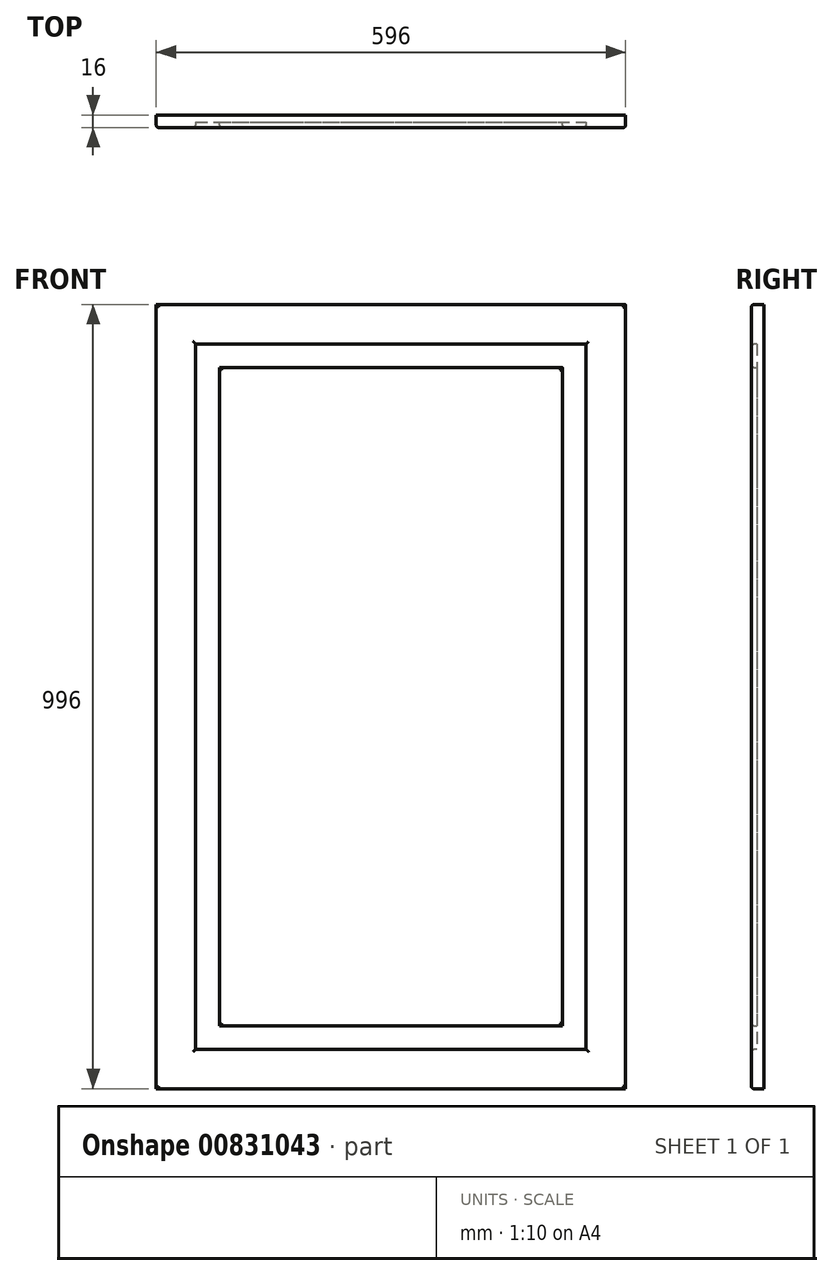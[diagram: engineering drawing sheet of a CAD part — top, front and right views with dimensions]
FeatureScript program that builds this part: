
annotation { "Feature Type Name" : "Feature", "Feature Type Description" : "" }
export const myFeature = defineFeature(function(context is Context, id is Id, definition is map)
    precondition{}
    {
        {
            var Q0;
            Q0=qCreatedBy(makeId("Front.planeOp"),FACE);
            var sketch = newSketch(context, id + "F0", { "sketchPlane" : qUnion([Q0])});
            skLineSegment(sketch, "E0.bottom", {"start": v(0, 0) * mm, "end": v(44.66, 0) * mm});
            skLineSegment(sketch, "E0.top", {"start": v(0, 33.8) * mm, "end": v(44.66, 33.8) * mm});
            skLineSegment(sketch, "E0.left", {"start": v(0, 0) * mm, "end": v(0, 33.8) * mm});
            skLineSegment(sketch, "E0.right", {"start": v(44.66, 0) * mm, "end": v(44.66, 33.8) * mm});
            skSolve(sketch);
        }
        {
            var Q0;
            Q0=makeQuery(id+"F0.imprint","IMPRINT",FACE,{"disambiguationData":[TD([[makeQuery(id+"F0.imprint","IMPRINT",EDGE,{"derivedFrom":sQuery(id+"F0.wireOp",EDGE,"E0.bottom")}),1.0]])]});
            extrude(context, id + "F1", {"entities" : qUnion([Q0]), "depth" : 16 * mm, "offsetDistance" : 25.4 * mm});
        }
        {
            var Q0;
            Q0=makeQuery(id+"F1.opExtrude","SWEPT_FACE",FACE,{"disambiguationData":[OSD([sQuery(id+"F0.wireOp",EDGE,"E0.bottom")])]});
            extrude(context, id + "F2", {"entities" : qUnion([Q0]), "operationType" : NewBodyOperationType.ADD, "oppositeDirection" : true, "depth" : 796 * mm, "offsetDistance" : 25 * mm});
        }
        {
            var Q0;
            {var subQ0=sQuery(id+"F0.wireOp",EDGE,"E0.left");Q0=makeQuery(id+"F2.boolean.opBoolean","MERGE",FACE,{"derivedFrom":[makeQuery(id+"F1.opExtrude","SWEPT_FACE",FACE,{"disambiguationData":[OSD([subQ0])]}),makeQuery(id+"F2.opExtrude","SWEPT_FACE",FACE,{"disambiguationData":[OSD([sQuery(id+"F0.wireOp",EDGE,"E0.bottom"),subQ0])]})]});}
            extrude(context, id + "F3", {"entities" : qUnion([Q0]), "operationType" : NewBodyOperationType.ADD, "oppositeDirection" : true, "depth" : 196 * mm, "offsetDistance" : 25 * mm});
        }
        {
            var Q0;
            {var subQ0=sQuery(id+"F0.wireOp",EDGE,"E0.left");var subQ1=sQuery(id+"F0.wireOp",EDGE,"E0.bottom");Q0=makeQuery(id+"F3.boolean.opBoolean","MERGE",FACE,{"derivedFrom":[makeQuery(id+"F2.boolean.opBoolean","MERGE",FACE,{"derivedFrom":[makeQuery(id+"F1.opExtrude","CAP_FACE",FACE,{"disambiguationData":[OSD([subQ1,sQuery(id+"F0.wireOp",EDGE,"E0.top"),subQ0,sQuery(id+"F0.wireOp",EDGE,"E0.right")])],"isStart":false}),makeQuery(id+"F2.opExtrude","SWEPT_FACE",FACE,{"disambiguationData":[OSD([subQ1]),TDD([makeQuery(id+"F1.opExtrude","CAP_EDGE",EDGE,{"disambiguationData":[OSD([subQ1])],"isStart":false})])]})]}),makeQuery(id+"F3.opExtrude","SWEPT_FACE",FACE,{"disambiguationData":[OSD([subQ1,subQ0]),TDD([makeQuery(id+"F2.boolean.opBoolean","MERGE",EDGE,{"derivedFrom":[makeQuery(id+"F1.opExtrude","CAP_EDGE",EDGE,{"disambiguationData":[OSD([subQ0])],"isStart":false}),makeQuery(id+"F2.opExtrude","SWEPT_EDGE",EDGE,{"disambiguationData":[OSD([subQ1,subQ0]),TDD([makeQuery(id+"F1.opExtrude","CAP_VERTEX",VERTEX,{"disambiguationData":[OSD([subQ1,subQ0])],"isStart":false})])]})]})])]})]});}
            var sketch = newSketch(context, id + "F4", { "sketchPlane" : qUnion([Q0])});
            skLineSegment(sketch, "E1.bottom", {"start": v(59.7, 646.67) * mm, "end": v(128.66, 646.67) * mm});
            skLineSegment(sketch, "E1.top", {"start": v(59.7, 152.97) * mm, "end": v(128.66, 152.97) * mm});
            skLineSegment(sketch, "E1.left", {"start": v(59.7, 646.67) * mm, "end": v(59.7, 152.97) * mm});
            skLineSegment(sketch, "E1.right", {"start": v(128.66, 646.67) * mm, "end": v(128.66, 152.97) * mm});
            skSolve(sketch);
        }
        {
            var Q0;
            Q0=makeQuery(id+"F4.imprint","IMPRINT",FACE,{"disambiguationData":[TD([[makeQuery(id+"F4.imprint","IMPRINT",EDGE,{"derivedFrom":sQuery(id+"F4.wireOp",EDGE,"E1.bottom")}),-1.0]])]});
            extrude(context, id + "F5", {"entities" : qUnion([Q0]), "operationType" : NewBodyOperationType.REMOVE, "oppositeDirection" : true, "depth" : 7 * mm, "offsetDistance" : 25 * mm});
        }
        {
            var Q0;
            Q0=makeQuery(id+"F5.boolean.opBoolean","COPY",FACE,{"derivedFrom":makeQuery(id+"F5.opExtrude","SWEPT_FACE",FACE,{"disambiguationData":[OSD([sQuery(id+"F4.wireOp",EDGE,"E1.left")])]})});
            extrude(context, id + "F6", {"entities" : qUnion([Q0]), "operationType" : NewBodyOperationType.REMOVE, "oppositeDirection" : true, "depth" : 9.7 * mm, "offsetDistance" : 25 * mm});
        }
        {
            var Q0;
            {var subQ0=sQuery(id+"F4.wireOp",EDGE,"E1.bottom");Q0=makeQuery(id+"F6.boolean.opBoolean","MERGE",FACE,{"derivedFrom":[makeQuery(id+"F5.boolean.opBoolean","COPY",FACE,{"derivedFrom":makeQuery(id+"F5.opExtrude","SWEPT_FACE",FACE,{"disambiguationData":[OSD([subQ0])]})}),makeQuery(id+"F6.opExtrude","SWEPT_FACE",FACE,{"disambiguationData":[OSD([subQ0,sQuery(id+"F4.wireOp",EDGE,"E1.left")])]})]});}
            extrude(context, id + "F7", {"entities" : qUnion([Q0]), "operationType" : NewBodyOperationType.ADD, "oppositeDirection" : true, "depth" : 99.33 * mm, "offsetDistance" : 25 * mm});
        }
        {
            var Q0;
            {var subQ0=sQuery(id+"F4.wireOp",EDGE,"E1.bottom");Q0=makeQuery(id+"F6.boolean.opBoolean","MERGE",FACE,{"derivedFrom":[makeQuery(id+"F5.boolean.opBoolean","COPY",FACE,{"derivedFrom":makeQuery(id+"F5.opExtrude","SWEPT_FACE",FACE,{"disambiguationData":[OSD([subQ0])]})}),makeQuery(id+"F6.opExtrude","SWEPT_FACE",FACE,{"disambiguationData":[OSD([subQ0,sQuery(id+"F4.wireOp",EDGE,"E1.left")])]})]});}
            extrude(context, id + "F8", {"entities" : qUnion([Q0]), "operationType" : NewBodyOperationType.REMOVE, "oppositeDirection" : true, "depth" : 99.33 * mm, "offsetDistance" : 25 * mm});
        }
        {
            var Q0;
            {var subQ0=sQuery(id+"F4.wireOp",EDGE,"E1.right");Q0=makeQuery(id+"F8.boolean.opBoolean","MERGE",FACE,{"derivedFrom":[makeQuery(id+"F5.boolean.opBoolean","COPY",FACE,{"derivedFrom":makeQuery(id+"F5.opExtrude","SWEPT_FACE",FACE,{"disambiguationData":[OSD([subQ0])]})}),makeQuery(id+"F8.opExtrude","SWEPT_FACE",FACE,{"disambiguationData":[OSD([sQuery(id+"F4.wireOp",EDGE,"E1.bottom"),subQ0])]})]});}
            extrude(context, id + "F9", {"entities" : qUnion([Q0]), "operationType" : NewBodyOperationType.REMOVE, "oppositeDirection" : true, "depth" : 17.34 * mm, "offsetDistance" : 25 * mm});
        }
        {
            var Q0;
            {var subQ0=sQuery(id+"F4.wireOp",EDGE,"E1.top");Q0=makeQuery(id+"F9.boolean.opBoolean","MERGE",FACE,{"derivedFrom":[makeQuery(id+"F6.boolean.opBoolean","MERGE",FACE,{"derivedFrom":[makeQuery(id+"F5.boolean.opBoolean","COPY",FACE,{"derivedFrom":makeQuery(id+"F5.opExtrude","SWEPT_FACE",FACE,{"disambiguationData":[OSD([subQ0])]})}),makeQuery(id+"F6.opExtrude","SWEPT_FACE",FACE,{"disambiguationData":[OSD([subQ0,sQuery(id+"F4.wireOp",EDGE,"E1.left")])]})]}),makeQuery(id+"F9.opExtrude","SWEPT_FACE",FACE,{"disambiguationData":[OSD([subQ0,sQuery(id+"F4.wireOp",EDGE,"E1.right")])]})]});}
            extrude(context, id + "F10", {"entities" : qUnion([Q0]), "operationType" : NewBodyOperationType.REMOVE, "oppositeDirection" : true, "depth" : 102.97 * mm, "offsetDistance" : 25 * mm});
        }
        {
            var Q0;
            {var subQ0=sQuery(id+"F4.wireOp",EDGE,"E1.right");var subQ1=sQuery(id+"F4.wireOp",EDGE,"E1.top");var subQ2=sQuery(id+"F4.wireOp",EDGE,"E1.left");var subQ3=sQuery(id+"F4.wireOp",EDGE,"E1.bottom");Q0=makeQuery(id+"F10.boolean.opBoolean","MERGE",FACE,{"derivedFrom":[makeQuery(id+"F9.boolean.opBoolean","MERGE",FACE,{"derivedFrom":[makeQuery(id+"F8.boolean.opBoolean","MERGE",FACE,{"derivedFrom":[makeQuery(id+"F6.boolean.opBoolean","MERGE",FACE,{"derivedFrom":[makeQuery(id+"F5.boolean.opBoolean","COPY",FACE,{"derivedFrom":makeQuery(id+"F5.opExtrude","CAP_FACE",FACE,{"disambiguationData":[OSD([subQ3,subQ1,subQ2,subQ0])],"isStart":false})}),makeQuery(id+"F6.opExtrude","SWEPT_FACE",FACE,{"disambiguationData":[OSD([subQ2]),TDD([makeQuery(id+"F5.boolean.opBoolean","COPY",EDGE,{"derivedFrom":makeQuery(id+"F5.opExtrude","CAP_EDGE",EDGE,{"disambiguationData":[OSD([subQ2])],"isStart":false})})])]})]}),makeQuery(id+"F8.opExtrude","SWEPT_FACE",FACE,{"disambiguationData":[OSD([subQ3,subQ2]),TDD([makeQuery(id+"F6.boolean.opBoolean","MERGE",EDGE,{"derivedFrom":[makeQuery(id+"F5.boolean.opBoolean","COPY",EDGE,{"derivedFrom":makeQuery(id+"F5.opExtrude","CAP_EDGE",EDGE,{"disambiguationData":[OSD([subQ3])],"isStart":false})}),makeQuery(id+"F6.opExtrude","SWEPT_EDGE",EDGE,{"disambiguationData":[OSD([subQ3,subQ2]),TDD([makeQuery(id+"F5.boolean.opBoolean","COPY",VERTEX,{"derivedFrom":makeQuery(id+"F5.opExtrude","CAP_VERTEX",VERTEX,{"disambiguationData":[OSD([subQ3,subQ2])],"isStart":false})})])]})]})])]})]}),makeQuery(id+"F9.opExtrude","SWEPT_FACE",FACE,{"disambiguationData":[OSD([subQ3,subQ0]),TDD([makeQuery(id+"F8.boolean.opBoolean","MERGE",EDGE,{"derivedFrom":[makeQuery(id+"F5.boolean.opBoolean","COPY",EDGE,{"derivedFrom":makeQuery(id+"F5.opExtrude","CAP_EDGE",EDGE,{"disambiguationData":[OSD([subQ0])],"isStart":false})}),makeQuery(id+"F8.opExtrude","SWEPT_EDGE",EDGE,{"disambiguationData":[OSD([subQ3,subQ0]),TDD([makeQuery(id+"F5.boolean.opBoolean","COPY",VERTEX,{"derivedFrom":makeQuery(id+"F5.opExtrude","CAP_VERTEX",VERTEX,{"disambiguationData":[OSD([subQ3,subQ0])],"isStart":false})})])]})]})])]})]}),makeQuery(id+"F10.opExtrude","SWEPT_FACE",FACE,{"disambiguationData":[OSD([subQ1,subQ2,subQ0]),TDD([makeQuery(id+"F9.boolean.opBoolean","MERGE",EDGE,{"derivedFrom":[makeQuery(id+"F6.boolean.opBoolean","MERGE",EDGE,{"derivedFrom":[makeQuery(id+"F5.boolean.opBoolean","COPY",EDGE,{"derivedFrom":makeQuery(id+"F5.opExtrude","CAP_EDGE",EDGE,{"disambiguationData":[OSD([subQ1])],"isStart":false})}),makeQuery(id+"F6.opExtrude","SWEPT_EDGE",EDGE,{"disambiguationData":[OSD([subQ1,subQ2]),TDD([makeQuery(id+"F5.boolean.opBoolean","COPY",VERTEX,{"derivedFrom":makeQuery(id+"F5.opExtrude","CAP_VERTEX",VERTEX,{"disambiguationData":[OSD([subQ1,subQ2])],"isStart":false})})])]})]}),makeQuery(id+"F9.opExtrude","SWEPT_EDGE",EDGE,{"disambiguationData":[OSD([subQ1,subQ0]),TDD([makeQuery(id+"F5.boolean.opBoolean","COPY",VERTEX,{"derivedFrom":makeQuery(id+"F5.opExtrude","CAP_VERTEX",VERTEX,{"disambiguationData":[OSD([subQ1,subQ0])],"isStart":false})})])]})]})])]})]});}
            var sketch = newSketch(context, id + "F11", { "sketchPlane" : qUnion([Q0])});
            skLineSegment(sketch, "E2.bottom", {"start": v(74.13, 678.73) * mm, "end": v(109.41, 678.73) * mm});
            skLineSegment(sketch, "E2.top", {"start": v(74.13, 186.63) * mm, "end": v(109.41, 186.63) * mm});
            skLineSegment(sketch, "E2.left", {"start": v(74.13, 678.73) * mm, "end": v(74.13, 186.63) * mm});
            skLineSegment(sketch, "E2.right", {"start": v(109.41, 678.73) * mm, "end": v(109.41, 186.63) * mm});
            skSolve(sketch);
        }
        {
            var Q0;
            Q0=makeQuery(id+"F11.imprint","IMPRINT",FACE,{"disambiguationData":[TD([[makeQuery(id+"F11.imprint","IMPRINT",EDGE,{"derivedFrom":sQuery(id+"F11.wireOp",EDGE,"E2.bottom")}),-1.0]])]});
            extrude(context, id + "F12", {"entities" : qUnion([Q0]), "operationType" : NewBodyOperationType.ADD, "depth" : 7 * mm, "offsetDistance" : 25 * mm});
        }
        {
            var Q0;
            Q0=makeQuery(id+"F12.opExtrude","SWEPT_FACE",FACE,{"disambiguationData":[OSD([sQuery(id+"F11.wireOp",EDGE,"E2.bottom")])]});
            extrude(context, id + "F13", {"entities" : qUnion([Q0]), "operationType" : NewBodyOperationType.ADD, "depth" : 37.27 * mm, "offsetDistance" : 25 * mm});
        }
        {
            var Q0;
            {var subQ0=sQuery(id+"F11.wireOp",EDGE,"E2.right");Q0=makeQuery(id+"F13.boolean.opBoolean","MERGE",FACE,{"derivedFrom":[makeQuery(id+"F12.opExtrude","SWEPT_FACE",FACE,{"disambiguationData":[OSD([subQ0])]}),makeQuery(id+"F13.opExtrude","SWEPT_FACE",FACE,{"disambiguationData":[OSD([sQuery(id+"F11.wireOp",EDGE,"E2.bottom"),subQ0])]})]});}
            extrude(context, id + "F14", {"entities" : qUnion([Q0]), "operationType" : NewBodyOperationType.ADD, "depth" : 6.58 * mm, "offsetDistance" : 25 * mm});
        }
        {
            var Q0;
            {var subQ0=sQuery(id+"F11.wireOp",EDGE,"E2.top");Q0=makeQuery(id+"F14.boolean.opBoolean","MERGE",FACE,{"derivedFrom":[makeQuery(id+"F12.opExtrude","SWEPT_FACE",FACE,{"disambiguationData":[OSD([subQ0])]}),makeQuery(id+"F14.opExtrude","SWEPT_FACE",FACE,{"disambiguationData":[OSD([subQ0,sQuery(id+"F11.wireOp",EDGE,"E2.right")])]})]});}
            extrude(context, id + "F15", {"entities" : qUnion([Q0]), "operationType" : NewBodyOperationType.ADD, "depth" : 106.63 * mm, "offsetDistance" : 25 * mm});
        }
        {
            var Q0;
            {var subQ0=sQuery(id+"F11.wireOp",EDGE,"E2.left");Q0=makeQuery(id+"F15.boolean.opBoolean","MERGE",FACE,{"derivedFrom":[makeQuery(id+"F13.boolean.opBoolean","MERGE",FACE,{"derivedFrom":[makeQuery(id+"F12.opExtrude","SWEPT_FACE",FACE,{"disambiguationData":[OSD([subQ0])]}),makeQuery(id+"F13.opExtrude","SWEPT_FACE",FACE,{"disambiguationData":[OSD([sQuery(id+"F11.wireOp",EDGE,"E2.bottom"),subQ0])]})]}),makeQuery(id+"F15.opExtrude","SWEPT_FACE",FACE,{"disambiguationData":[OSD([sQuery(id+"F11.wireOp",EDGE,"E2.top"),subQ0])]})]});}
            extrude(context, id + "F16", {"entities" : qUnion([Q0]), "operationType" : NewBodyOperationType.REMOVE, "oppositeDirection" : true, "depth" : 5.87 * mm, "offsetDistance" : 25 * mm});
        }
        {
            var Q0;
            Q0=makeQuery(id+"F3.opExtrude","CAP_FACE",FACE,{"disambiguationData":[OSD([sQuery(id+"F0.wireOp",EDGE,"E0.bottom"),sQuery(id+"F0.wireOp",EDGE,"E0.left")])],"isStart":false});
            extrude(context, id + "F17", {"entities" : qUnion([Q0]), "operationType" : NewBodyOperationType.ADD, "depth" : 200 * mm, "offsetDistance" : 25 * mm});
        }
        {
            var Q0;
            {var subQ0=sQuery(id+"F4.wireOp",EDGE,"E1.right");Q0=makeQuery(id+"F10.boolean.opBoolean","MERGE",FACE,{"derivedFrom":[makeQuery(id+"F9.boolean.opBoolean","COPY",FACE,{"derivedFrom":makeQuery(id+"F9.opExtrude","CAP_FACE",FACE,{"disambiguationData":[OSD([sQuery(id+"F4.wireOp",EDGE,"E1.bottom"),subQ0])],"isStart":false})}),makeQuery(id+"F10.opExtrude","SWEPT_FACE",FACE,{"disambiguationData":[OSD([sQuery(id+"F4.wireOp",EDGE,"E1.top"),subQ0])]})]});}
            extrude(context, id + "F18", {"entities" : qUnion([Q0]), "operationType" : NewBodyOperationType.REMOVE, "oppositeDirection" : true, "depth" : 200 * mm, "offsetDistance" : 25 * mm});
        }
        {
            var Q0;
            {var subQ0=sQuery(id+"F11.wireOp",EDGE,"E2.right");var subQ1=sQuery(id+"F11.wireOp",EDGE,"E2.top");Q0=makeQuery(id+"F15.boolean.opBoolean","MERGE",FACE,{"derivedFrom":[makeQuery(id+"F14.opExtrude","CAP_FACE",FACE,{"disambiguationData":[OSD([sQuery(id+"F11.wireOp",EDGE,"E2.bottom"),subQ0])],"isStart":false}),makeQuery(id+"F15.opExtrude","SWEPT_FACE",FACE,{"disambiguationData":[OSD([subQ1,subQ0]),TDD([makeQuery(id+"F14.opExtrude","CAP_EDGE",EDGE,{"disambiguationData":[OSD([subQ1,subQ0])],"isStart":false})])]})]});}
            extrude(context, id + "F19", {"entities" : qUnion([Q0]), "operationType" : NewBodyOperationType.ADD, "depth" : 200 * mm, "offsetDistance" : 25 * mm});
        }
        {
            var Q0;
            Q0=makeQuery(id+"F17.opExtrude","CAP_FACE",FACE,{"disambiguationData":[OSD([sQuery(id+"F0.wireOp",EDGE,"E0.bottom"),sQuery(id+"F0.wireOp",EDGE,"E0.left")])],"isStart":false});
            extrude(context, id + "F20", {"entities" : qUnion([Q0]), "operationType" : NewBodyOperationType.ADD, "depth" : 200 * mm, "offsetDistance" : 25 * mm});
        }
        {
            var Q0;
            Q0=makeQuery(id+"F18.boolean.opBoolean","COPY",FACE,{"derivedFrom":makeQuery(id+"F18.opExtrude","CAP_FACE",FACE,{"disambiguationData":[OSD([sQuery(id+"F4.wireOp",EDGE,"E1.bottom"),sQuery(id+"F4.wireOp",EDGE,"E1.top"),sQuery(id+"F4.wireOp",EDGE,"E1.right")])],"isStart":false})});
            extrude(context, id + "F21", {"entities" : qUnion([Q0]), "operationType" : NewBodyOperationType.REMOVE, "oppositeDirection" : true, "depth" : 200 * mm, "offsetDistance" : 25 * mm});
        }
        {
            var Q0;
            Q0=makeQuery(id+"F19.opExtrude","CAP_FACE",FACE,{"disambiguationData":[OSD([sQuery(id+"F11.wireOp",EDGE,"E2.bottom"),sQuery(id+"F11.wireOp",EDGE,"E2.top"),sQuery(id+"F11.wireOp",EDGE,"E2.right")])],"isStart":false});
            extrude(context, id + "F22", {"entities" : qUnion([Q0]), "operationType" : NewBodyOperationType.ADD, "depth" : 200 * mm, "offsetDistance" : 25 * mm});
        }
        {
            var Q0;
            {var subQ0=sQuery(id+"F0.wireOp",EDGE,"E0.left");var subQ1=sQuery(id+"F0.wireOp",EDGE,"E0.bottom");var subQ2=makeQuery(id+"F2.opExtrude","CAP_EDGE",EDGE,{"disambiguationData":[OSD([subQ1,subQ0])],"isStart":false});var subQ3=makeQuery(id+"F3.opExtrude","CAP_EDGE",EDGE,{"disambiguationData":[OSD([subQ1,subQ0]),TDD([subQ2])],"isStart":false});Q0=makeQuery(id+"F20.boolean.opBoolean","MERGE",FACE,{"derivedFrom":[makeQuery(id+"F17.boolean.opBoolean","MERGE",FACE,{"derivedFrom":[makeQuery(id+"F3.boolean.opBoolean","MERGE",FACE,{"derivedFrom":[makeQuery(id+"F2.opExtrude","CAP_FACE",FACE,{"disambiguationData":[OSD([subQ1])],"isStart":false}),makeQuery(id+"F3.opExtrude","SWEPT_FACE",FACE,{"disambiguationData":[OSD([subQ1,subQ0]),TDD([subQ2])]})]}),makeQuery(id+"F17.opExtrude","SWEPT_FACE",FACE,{"disambiguationData":[OSD([subQ1,subQ0]),TDD([subQ3])]})]}),makeQuery(id+"F20.opExtrude","SWEPT_FACE",FACE,{"disambiguationData":[OSD([subQ1,subQ0]),TDD([makeQuery(id+"F17.opExtrude","CAP_EDGE",EDGE,{"disambiguationData":[OSD([subQ1,subQ0]),TDD([subQ3])],"isStart":false})])]})]});}
            extrude(context, id + "F23", {"entities" : qUnion([Q0]), "operationType" : NewBodyOperationType.ADD, "depth" : 200 * mm, "offsetDistance" : 25 * mm});
        }
        {
            var Q0;
            {var subQ0=sQuery(id+"F4.wireOp",EDGE,"E1.right");var subQ1=sQuery(id+"F4.wireOp",EDGE,"E1.bottom");Q0=makeQuery(id+"F21.boolean.opBoolean","MERGE",FACE,{"derivedFrom":[makeQuery(id+"F18.boolean.opBoolean","MERGE",FACE,{"derivedFrom":[makeQuery(id+"F9.boolean.opBoolean","MERGE",FACE,{"derivedFrom":[makeQuery(id+"F8.boolean.opBoolean","COPY",FACE,{"derivedFrom":makeQuery(id+"F8.opExtrude","CAP_FACE",FACE,{"disambiguationData":[OSD([subQ1,sQuery(id+"F4.wireOp",EDGE,"E1.left")])],"isStart":false})}),makeQuery(id+"F9.opExtrude","SWEPT_FACE",FACE,{"disambiguationData":[OSD([subQ1,subQ0]),TDD([makeQuery(id+"F8.boolean.opBoolean","COPY",EDGE,{"derivedFrom":makeQuery(id+"F8.opExtrude","CAP_EDGE",EDGE,{"disambiguationData":[OSD([subQ1,subQ0])],"isStart":false})})])]})]}),makeQuery(id+"F18.opExtrude","SWEPT_FACE",FACE,{"disambiguationData":[OSD([subQ1,subQ0])]})]}),makeQuery(id+"F21.opExtrude","SWEPT_FACE",FACE,{"disambiguationData":[OSD([subQ1,subQ0])]})]});}
            extrude(context, id + "F24", {"entities" : qUnion([Q0]), "operationType" : NewBodyOperationType.REMOVE, "oppositeDirection" : true, "depth" : 200 * mm, "offsetDistance" : 25 * mm});
        }
        {
            var Q0;
            {var subQ0=sQuery(id+"F11.wireOp",EDGE,"E2.right");var subQ1=sQuery(id+"F11.wireOp",EDGE,"E2.bottom");Q0=makeQuery(id+"F22.boolean.opBoolean","MERGE",FACE,{"derivedFrom":[makeQuery(id+"F19.boolean.opBoolean","MERGE",FACE,{"derivedFrom":[makeQuery(id+"F14.boolean.opBoolean","MERGE",FACE,{"derivedFrom":[makeQuery(id+"F13.opExtrude","CAP_FACE",FACE,{"disambiguationData":[OSD([subQ1])],"isStart":false}),makeQuery(id+"F14.opExtrude","SWEPT_FACE",FACE,{"disambiguationData":[OSD([subQ1,subQ0]),TDD([makeQuery(id+"F13.opExtrude","CAP_EDGE",EDGE,{"disambiguationData":[OSD([subQ1,subQ0])],"isStart":false})])]})]}),makeQuery(id+"F19.opExtrude","SWEPT_FACE",FACE,{"disambiguationData":[OSD([subQ1,subQ0])]})]}),makeQuery(id+"F22.opExtrude","SWEPT_FACE",FACE,{"disambiguationData":[OSD([subQ1,subQ0])]})]});}
            extrude(context, id + "F25", {"entities" : qUnion([Q0]), "operationType" : NewBodyOperationType.ADD, "depth" : 200 * mm, "offsetDistance" : 25 * mm});
        }
        {
            var Q0;
            {var subQ0=sQuery(id+"F0.wireOp",EDGE,"E0.left");var subQ1=sQuery(id+"F0.wireOp",EDGE,"E0.bottom");var subQ2=makeQuery(id+"F1.opExtrude","CAP_VERTEX",VERTEX,{"disambiguationData":[OSD([subQ1,subQ0])],"isStart":false});var subQ3=makeQuery(id+"F2.opExtrude","CAP_VERTEX",VERTEX,{"disambiguationData":[OSD([subQ1,subQ0]),TDD([subQ2])],"isStart":false});var subQ4=makeQuery(id+"F3.opExtrude","CAP_VERTEX",VERTEX,{"disambiguationData":[OSD([subQ1,subQ0]),TDD([subQ3])],"isStart":false});var subQ5=makeQuery(id+"F1.opExtrude","CAP_EDGE",EDGE,{"disambiguationData":[OSD([subQ1])],"isStart":false});var subQ6=makeQuery(id+"F2.boolean.opBoolean","MERGE",EDGE,{"derivedFrom":[makeQuery(id+"F1.opExtrude","CAP_EDGE",EDGE,{"disambiguationData":[OSD([subQ0])],"isStart":false}),makeQuery(id+"F2.opExtrude","SWEPT_EDGE",EDGE,{"disambiguationData":[OSD([subQ1,subQ0]),TDD([subQ2])]})]});var subQ7=makeQuery(id+"F3.opExtrude","CAP_EDGE",EDGE,{"disambiguationData":[OSD([subQ1,subQ0]),TDD([subQ6])],"isStart":false});Q0=makeQuery(id+"F23.boolean.opBoolean","MERGE",FACE,{"derivedFrom":[makeQuery(id+"F20.boolean.opBoolean","MERGE",FACE,{"derivedFrom":[makeQuery(id+"F17.boolean.opBoolean","MERGE",FACE,{"derivedFrom":[makeQuery(id+"F3.boolean.opBoolean","MERGE",FACE,{"derivedFrom":[makeQuery(id+"F2.boolean.opBoolean","MERGE",FACE,{"derivedFrom":[makeQuery(id+"F1.opExtrude","CAP_FACE",FACE,{"disambiguationData":[OSD([subQ1,sQuery(id+"F0.wireOp",EDGE,"E0.top"),subQ0,sQuery(id+"F0.wireOp",EDGE,"E0.right")])],"isStart":false}),makeQuery(id+"F2.opExtrude","SWEPT_FACE",FACE,{"disambiguationData":[OSD([subQ1]),TDD([subQ5])]})]}),makeQuery(id+"F3.opExtrude","SWEPT_FACE",FACE,{"disambiguationData":[OSD([subQ1,subQ0]),TDD([subQ6])]})]}),makeQuery(id+"F17.opExtrude","SWEPT_FACE",FACE,{"disambiguationData":[OSD([subQ1,subQ0]),TDD([subQ7])]})]}),makeQuery(id+"F20.opExtrude","SWEPT_FACE",FACE,{"disambiguationData":[OSD([subQ1,subQ0]),TDD([makeQuery(id+"F17.opExtrude","CAP_EDGE",EDGE,{"disambiguationData":[OSD([subQ1,subQ0]),TDD([subQ7])],"isStart":false})])]})]}),makeQuery(id+"F23.opExtrude","SWEPT_FACE",FACE,{"disambiguationData":[OSD([subQ1,subQ0]),TDD([makeQuery(id+"F20.boolean.opBoolean","MERGE",EDGE,{"derivedFrom":[makeQuery(id+"F17.boolean.opBoolean","MERGE",EDGE,{"derivedFrom":[makeQuery(id+"F3.boolean.opBoolean","MERGE",EDGE,{"derivedFrom":[makeQuery(id+"F2.opExtrude","CAP_EDGE",EDGE,{"disambiguationData":[OSD([subQ1]),TDD([subQ5])],"isStart":false}),makeQuery(id+"F3.opExtrude","SWEPT_EDGE",EDGE,{"disambiguationData":[OSD([subQ1,subQ0]),TDD([subQ3])]})]}),makeQuery(id+"F17.opExtrude","SWEPT_EDGE",EDGE,{"disambiguationData":[OSD([subQ1,subQ0]),TDD([subQ4])]})]}),makeQuery(id+"F20.opExtrude","SWEPT_EDGE",EDGE,{"disambiguationData":[OSD([subQ1,subQ0]),TDD([makeQuery(id+"F17.opExtrude","CAP_VERTEX",VERTEX,{"disambiguationData":[OSD([subQ1,subQ0]),TDD([subQ4])],"isStart":false})])]})]})])]})]});}
            var Q1;
            {var subQ0=sQuery(id+"F11.wireOp",EDGE,"E2.right");var subQ1=sQuery(id+"F11.wireOp",EDGE,"E2.bottom");var subQ2=makeQuery(id+"F12.opExtrude","CAP_VERTEX",VERTEX,{"disambiguationData":[OSD([subQ1,subQ0])],"isStart":false});var subQ3=makeQuery(id+"F13.opExtrude","CAP_VERTEX",VERTEX,{"disambiguationData":[OSD([subQ1,subQ0]),TDD([subQ2])],"isStart":false});var subQ4=makeQuery(id+"F14.opExtrude","CAP_VERTEX",VERTEX,{"disambiguationData":[OSD([subQ1,subQ0]),TDD([subQ3])],"isStart":false});var subQ5=makeQuery(id+"F12.opExtrude","CAP_EDGE",EDGE,{"disambiguationData":[OSD([subQ1])],"isStart":false});var subQ6=sQuery(id+"F11.wireOp",EDGE,"E2.top");var subQ7=makeQuery(id+"F12.opExtrude","CAP_VERTEX",VERTEX,{"disambiguationData":[OSD([subQ6,subQ0])],"isStart":false});var subQ8=makeQuery(id+"F13.boolean.opBoolean","MERGE",EDGE,{"derivedFrom":[makeQuery(id+"F12.opExtrude","CAP_EDGE",EDGE,{"disambiguationData":[OSD([subQ0])],"isStart":false}),makeQuery(id+"F13.opExtrude","SWEPT_EDGE",EDGE,{"disambiguationData":[OSD([subQ1,subQ0]),TDD([subQ2])]})]});var subQ9=makeQuery(id+"F15.boolean.opBoolean","MERGE",EDGE,{"derivedFrom":[makeQuery(id+"F14.opExtrude","CAP_EDGE",EDGE,{"disambiguationData":[OSD([subQ1,subQ0]),TDD([subQ8])],"isStart":false}),makeQuery(id+"F15.opExtrude","SWEPT_EDGE",EDGE,{"disambiguationData":[OSD([subQ6,subQ0]),TDD([makeQuery(id+"F14.opExtrude","CAP_VERTEX",VERTEX,{"disambiguationData":[OSD([subQ6,subQ0]),TDD([subQ7])],"isStart":false})])]})]});Q1=makeQuery(id+"F25.boolean.opBoolean","MERGE",FACE,{"derivedFrom":[makeQuery(id+"F22.boolean.opBoolean","MERGE",FACE,{"derivedFrom":[makeQuery(id+"F19.boolean.opBoolean","MERGE",FACE,{"derivedFrom":[makeQuery(id+"F15.boolean.opBoolean","MERGE",FACE,{"derivedFrom":[makeQuery(id+"F14.boolean.opBoolean","MERGE",FACE,{"derivedFrom":[makeQuery(id+"F13.boolean.opBoolean","MERGE",FACE,{"derivedFrom":[makeQuery(id+"F12.opExtrude","CAP_FACE",FACE,{"disambiguationData":[OSD([subQ1,subQ6,sQuery(id+"F11.wireOp",EDGE,"E2.left"),subQ0])],"isStart":false}),makeQuery(id+"F13.opExtrude","SWEPT_FACE",FACE,{"disambiguationData":[OSD([subQ1]),TDD([subQ5])]})]}),makeQuery(id+"F14.opExtrude","SWEPT_FACE",FACE,{"disambiguationData":[OSD([subQ1,subQ0]),TDD([subQ8])]})]}),makeQuery(id+"F15.opExtrude","SWEPT_FACE",FACE,{"disambiguationData":[OSD([subQ6,subQ0]),TDD([makeQuery(id+"F14.boolean.opBoolean","MERGE",EDGE,{"derivedFrom":[makeQuery(id+"F12.opExtrude","CAP_EDGE",EDGE,{"disambiguationData":[OSD([subQ6])],"isStart":false}),makeQuery(id+"F14.opExtrude","SWEPT_EDGE",EDGE,{"disambiguationData":[OSD([subQ6,subQ0]),TDD([subQ7])]})]})])]})]}),makeQuery(id+"F19.opExtrude","SWEPT_FACE",FACE,{"disambiguationData":[OSD([subQ1,subQ6,subQ0]),TDD([subQ9])]})]}),makeQuery(id+"F22.opExtrude","SWEPT_FACE",FACE,{"disambiguationData":[OSD([subQ1,subQ6,subQ0]),TDD([makeQuery(id+"F19.opExtrude","CAP_EDGE",EDGE,{"disambiguationData":[OSD([subQ1,subQ6,subQ0]),TDD([subQ9])],"isStart":false})])]})]}),makeQuery(id+"F25.opExtrude","SWEPT_FACE",FACE,{"disambiguationData":[OSD([subQ1,subQ0]),TDD([makeQuery(id+"F22.boolean.opBoolean","MERGE",EDGE,{"derivedFrom":[makeQuery(id+"F19.boolean.opBoolean","MERGE",EDGE,{"derivedFrom":[makeQuery(id+"F14.boolean.opBoolean","MERGE",EDGE,{"derivedFrom":[makeQuery(id+"F13.opExtrude","CAP_EDGE",EDGE,{"disambiguationData":[OSD([subQ1]),TDD([subQ5])],"isStart":false}),makeQuery(id+"F14.opExtrude","SWEPT_EDGE",EDGE,{"disambiguationData":[OSD([subQ1,subQ0]),TDD([subQ3])]})]}),makeQuery(id+"F19.opExtrude","SWEPT_EDGE",EDGE,{"disambiguationData":[OSD([subQ1,subQ0]),TDD([subQ4])]})]}),makeQuery(id+"F22.opExtrude","SWEPT_EDGE",EDGE,{"disambiguationData":[OSD([subQ1,subQ0]),TDD([makeQuery(id+"F19.opExtrude","CAP_VERTEX",VERTEX,{"disambiguationData":[OSD([subQ1,subQ0]),TDD([subQ4])],"isStart":false})])]})]})])]})]});}
            fillet(context, id + "F26", {"entities" : qUnion([Q0, Q1]), "radius" : 3 * mm, "tangentPropagation" : true, "allowEdgeOverflow" : false});
        }
    });
